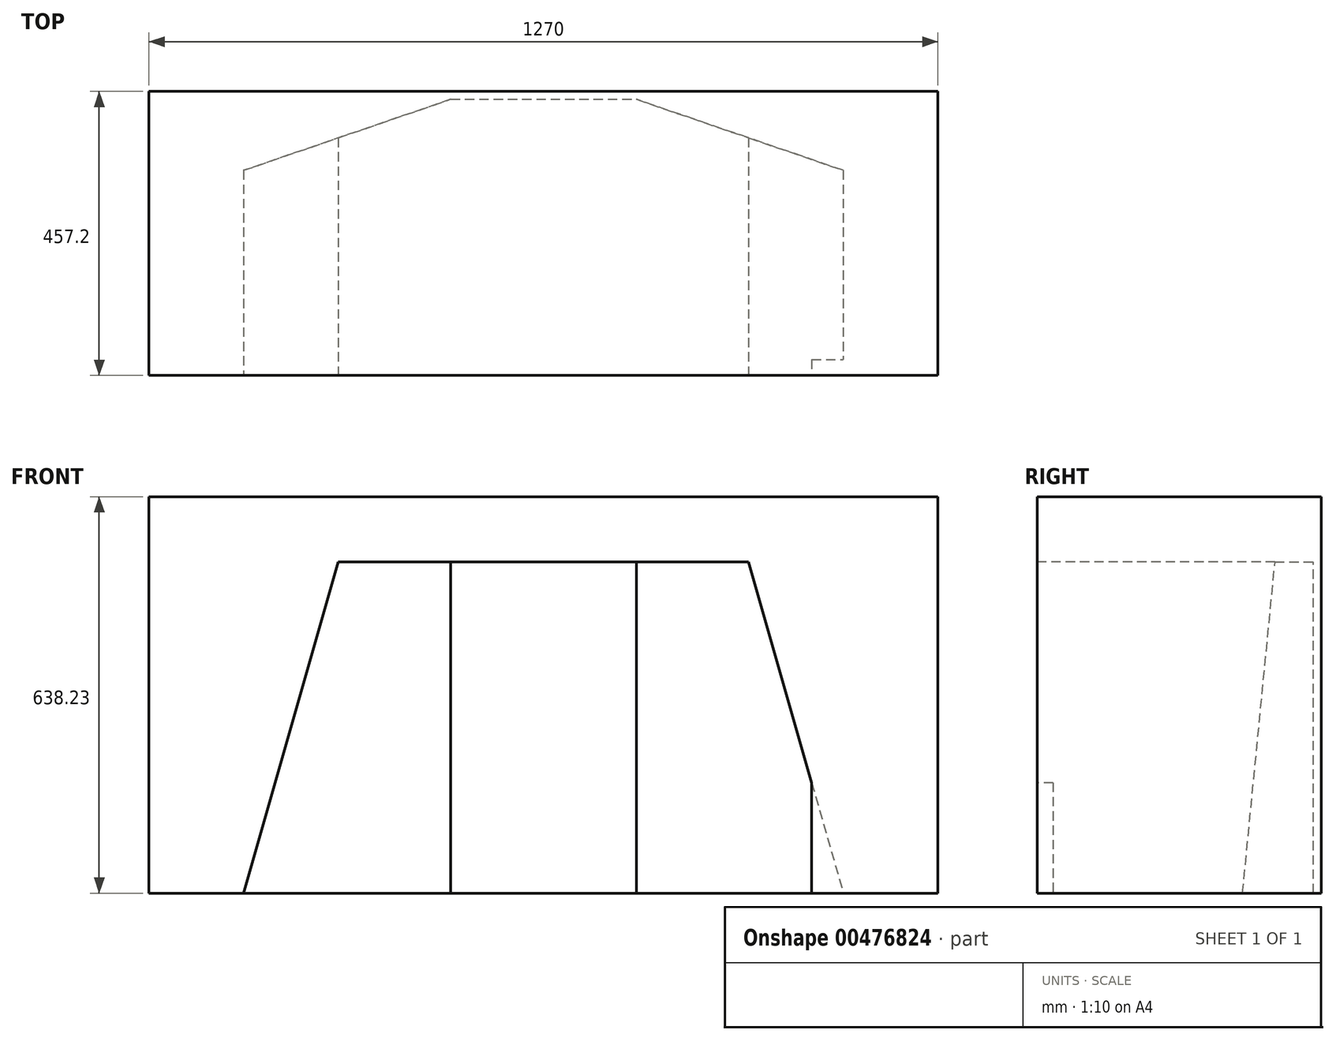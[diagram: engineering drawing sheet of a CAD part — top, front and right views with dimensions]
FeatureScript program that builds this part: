
annotation { "Feature Type Name" : "Feature", "Feature Type Description" : "" }
export const myFeature = defineFeature(function(context is Context, id is Id, definition is map)
    precondition{}
    {
        {
            var Q0;
            Q0=qCreatedBy(makeId("Front.planeOp"),FACE);
            var sketch = newSketch(context, id + "F0", { "sketchPlane" : qUnion([Q0])});
            skCircle(sketch, "E0", {"center": v(0, 0) * mm, "radius": 381 * mm, "construction": true});
            skLineSegment(sketch, "E1", {"start": v(-381, 0) * mm, "end": v(381, 0) * mm, "construction": true});
            skLineSegment(sketch, "E2", {"start": v(-469.9, 25.4) * mm, "end": v(-622.3, 25.4) * mm});
            skLineSegment(sketch, "E3", {"start": v(-469.9, 25.4) * mm, "end": v(-317.5, 558.8) * mm});
            skLineSegment(sketch, "E4", {"start": v(-317.5, 558.8) * mm, "end": v(342.9, 558.8) * mm});
            skLineSegment(sketch, "E5", {"start": v(342.9, 558.8) * mm, "end": v(495.3, 25.4) * mm});
            skLineSegment(sketch, "E6", {"start": v(495.3, 25.4) * mm, "end": v(647.7, 25.4) * mm});
            skLineSegment(sketch, "E7", {"start": v(-368.3, 381) * mm, "end": v(393.7, 381) * mm, "construction": true});
            skLineSegment(sketch, "E8", {"start": v(-368.3, 381) * mm, "end": v(12.7, 558.8) * mm, "construction": true});
            skLineSegment(sketch, "E9", {"start": v(12.7, 558.8) * mm, "end": v(393.7, 381) * mm, "construction": true});
            skLineSegment(sketch, "E10", {"start": v(-622.3, 25.4) * mm, "end": v(-622.3, 663.63) * mm});
            skLineSegment(sketch, "E11", {"start": v(-622.3, 663.63) * mm, "end": v(647.7, 663.63) * mm});
            skLineSegment(sketch, "E12", {"start": v(647.7, 663.63) * mm, "end": v(647.7, 25.4) * mm});
            skPoint(sketch, "E13", {"position": v(12.7, 663.63) * mm});
            skLineSegment(sketch, "E14", {"start": v(12.7, 558.8) * mm, "end": v(12.7, 0) * mm, "construction": true});
            skSolve(sketch);
        }
        {
            var Q0;
            Q0 = qSketchRegion(id + "F0", true);
            extrude(context, id + "F1", {"entities" : qUnion([Q0]), "oppositeDirection" : true, "depth" : 457.2 * mm});
        }
        {
            var Q0;
            Q0=makeQuery(id+"F1.opExtrude","CAP_FACE",FACE,{"disambiguationData":[OSD([sQuery(id+"F0.wireOp",EDGE,"E2"),sQuery(id+"F0.wireOp",EDGE,"E3"),sQuery(id+"F0.wireOp",EDGE,"E4"),sQuery(id+"F0.wireOp",EDGE,"E5"),sQuery(id+"F0.wireOp",EDGE,"E6"),sQuery(id+"F0.wireOp",EDGE,"E10"),sQuery(id+"F0.wireOp",EDGE,"E11"),sQuery(id+"F0.wireOp",EDGE,"E12")])],"isStart":true});
            var sketch = newSketch(context, id + "F2", { "sketchPlane" : qUnion([Q0])});
            skLineSegment(sketch, "E15", {"start": v(495.3, 25.4) * mm, "end": v(444.5, 25.4) * mm});
            skLineSegment(sketch, "E16", {"start": v(444.5, 25.4) * mm, "end": v(444.5, 203.2) * mm});
            skSolve(sketch);
        }
        {
            var Q0;
            {var subQ0=sQuery(id+"F2.wireOp",EDGE,"E15");Q0=makeQuery(id+"F2.imprint","IMPRINT",FACE,{"disambiguationData":[TD([[makeQuery(id+"F2.imprint","IMPRINT",EDGE,{"derivedFrom":subQ0}),-1.0]])]});}
            extrude(context, id + "F3", {"entities" : qUnion([Q0]), "operationType" : NewBodyOperationType.ADD, "oppositeDirection" : true, "depth" : 25.4 * mm});
        }
        {
            var Q0;
            Q0=makeQuery(id+"F1.opExtrude","SWEPT_FACE",FACE,{"disambiguationData":[OSD([sQuery(id+"F0.wireOp",EDGE,"E11")])]});
            var sketch = newSketch(context, id + "F4", { "sketchPlane" : qUnion([Q0])});
            skLineSegment(sketch, "E17", {"start": v(-469.9, 457.2) * mm, "end": v(495.3, 457.2) * mm});
            skLineSegment(sketch, "E18", {"start": v(495.3, 457.2) * mm, "end": v(495.3, 330.2) * mm});
            skLineSegment(sketch, "E19", {"start": v(495.3, 330.2) * mm, "end": v(162.04, 444.5) * mm});
            skLineSegment(sketch, "E20", {"start": v(162.04, 444.5) * mm, "end": v(-136.64, 444.5) * mm});
            skLineSegment(sketch, "E21", {"start": v(-136.64, 444.5) * mm, "end": v(-469.9, 330.2) * mm});
            skLineSegment(sketch, "E22", {"start": v(-469.9, 330.2) * mm, "end": v(-469.9, 457.2) * mm});
            skSolve(sketch);
        }
        {
            var Q0;
            Q0=makeQuery(id+"F4.imprint","IMPRINT",FACE,{"disambiguationData":[TD([[makeQuery(id+"F4.imprint","IMPRINT",EDGE,{"derivedFrom":sQuery(id+"F4.wireOp",EDGE,"E17")}),-1.0]])]});
            var Q1;
            Q1=makeQuery(id+"F3.boolean.opBoolean","MERGE",FACE,{"derivedFrom":[makeQuery(id+"F1.opExtrude","SWEPT_FACE",FACE,{"disambiguationData":[OSD([sQuery(id+"F0.wireOp",EDGE,"E6")])]}),makeQuery(id+"F3.opExtrude","SWEPT_FACE",FACE,{"disambiguationData":[OSD([sQuery(id+"F2.wireOp",EDGE,"E15")])]})]});
            extrude(context, id + "F5", {"entities" : qUnion([Q0]), "operationType" : NewBodyOperationType.ADD, "endBound" : BoundingType.UP_TO_SURFACE, "oppositeDirection" : true, "endBoundEntityFace" : qUnion([Q1]), "depth" : 370.84 * mm});
        }
    });
